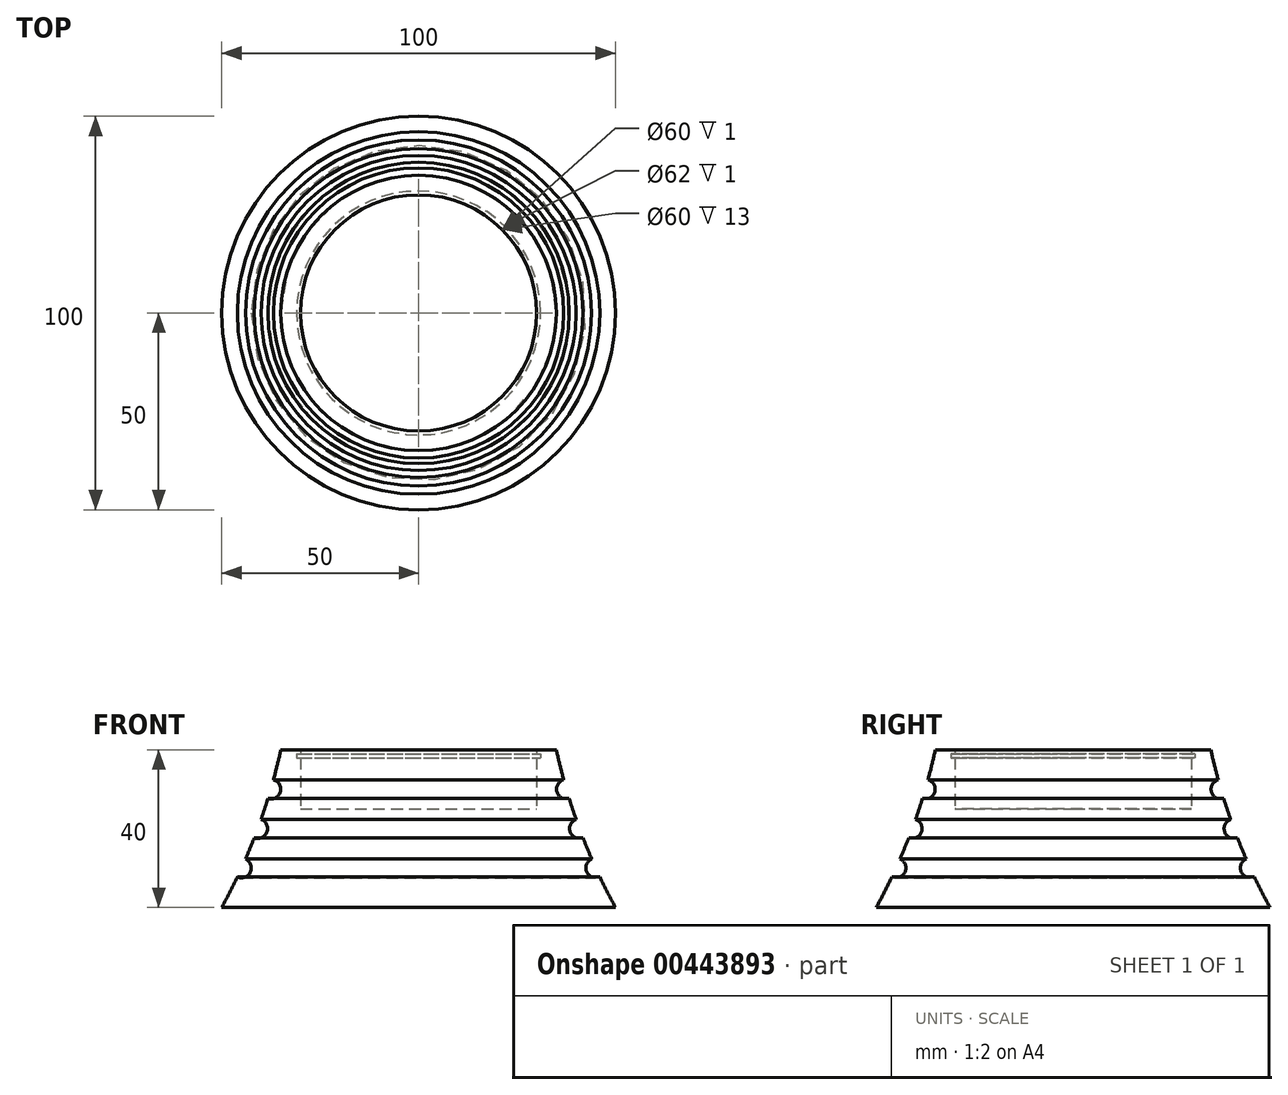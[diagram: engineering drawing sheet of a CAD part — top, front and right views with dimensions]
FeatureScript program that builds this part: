
annotation { "Feature Type Name" : "Feature", "Feature Type Description" : "" }
export const myFeature = defineFeature(function(context is Context, id is Id, definition is map)
    precondition{}
    {
        {
            var Q0;
            Q0=qCreatedBy(makeId("Front.planeOp"),FACE);
            var sketch = newSketch(context, id + "F0", { "sketchPlane" : qUnion([Q0])});
            skLineSegment(sketch, "E0", {"start": v(0, 0) * mm, "end": v(0, 25) * mm});
            skLineSegment(sketch, "E1", {"start": v(0, 25) * mm, "end": v(30, 25) * mm});
            skLineSegment(sketch, "E2", {"start": v(30, 25) * mm, "end": v(30, 38) * mm});
            skLineSegment(sketch, "E3", {"start": v(30, 40) * mm, "end": v(35, 40) * mm});
            skLineSegment(sketch, "E4", {"start": v(0, 0) * mm, "end": v(50, 0) * mm});
            skArc(sketch, "E5", {"start": v(35, 40) * mm, "mid": v(35.89, 36.2) * mm, "end": v(36.87, 32.4) * mm});
            skArc(sketch, "E6", {"start": v(36.87, 32.4) * mm, "mid": v(35.16, 29.3) * mm, "end": v(38.28, 27.6) * mm});
            skArc(sketch, "E7", {"start": v(40.02, 22.35) * mm, "mid": v(38.52, 19.13) * mm, "end": v(41.76, 17.66) * mm});
            skArc(sketch, "E8", {"start": v(43.97, 12.28) * mm, "mid": v(42.72, 8.96) * mm, "end": v(46.05, 7.73) * mm});
            skArc(sketch, "E9.trimOffspring", {"start": v(38.28, 27.6) * mm, "mid": v(39.12, 24.97) * mm, "end": v(40.02, 22.35) * mm});
            skArc(sketch, "E10.trimOffspring", {"start": v(41.76, 17.66) * mm, "mid": v(42.84, 14.96) * mm, "end": v(43.97, 12.28) * mm});
            skArc(sketch, "E11.trimOffspring", {"start": v(46.05, 7.73) * mm, "mid": v(47.97, 3.84) * mm, "end": v(50, 0) * mm});
            skLineSegment(sketch, "E12.bottom", {"start": v(30, 39) * mm, "end": v(31, 39) * mm});
            skLineSegment(sketch, "E12.top", {"start": v(30, 38) * mm, "end": v(31, 38) * mm});
            skLineSegment(sketch, "E12.right", {"start": v(31, 39) * mm, "end": v(31, 38) * mm});
            skLineSegment(sketch, "E13.trimOffspring", {"start": v(30, 39) * mm, "end": v(30, 40) * mm});
            skSolve(sketch);
        }
        {
            var Q0;
            Q0=makeQuery(id+"F0.imprint","IMPRINT",FACE,{"disambiguationData":[TD([[makeQuery(id+"F0.imprint","IMPRINT",EDGE,{"derivedFrom":sQuery(id+"F0.wireOp",EDGE,"E0")}),-1.0]])]});
            var Q1;
            Q1=sQuery(id+"F0.wireOp",EDGE,"E0");
            revolve(context, id + "F1", {"entities" : qUnion([Q0]), "axis" : qUnion([Q1]), "revolveType" : RevolveType.FULL});
        }
    });
